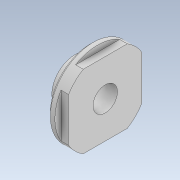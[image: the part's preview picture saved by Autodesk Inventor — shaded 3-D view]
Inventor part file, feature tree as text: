
AUTODESK INVENTOR PART (.ipt)
format: ipt  version: 2021 (Build 250183000, 183)  size: 128,512 bytes
history: native  units: mm
features: sketch x2, other x1, revolve x1, fillet x1, chamfer x1, extrude x1
ambient origin geometry x8: Origin, YZ Plane, XZ Plane, XY Plane, X Axis, Y Axis, Z Axis, Center Point
bodies: Body1 (feature_tree)
feature tree (7):
  other  "Sólido1"
  revolve  "Revolución1"  [1 undecoded]
  fillet  "Empalme1"  Radius=28.0mm
  chamfer  "Chaflán1"  Distance=8.0mm
  extrude  "Extrusión1"  TaperAngle=90.0deg  [1 undecoded]
  sketch  "Boceto1"  dims[d0=5.0mm d1=5.0mm d3=28.0mm]
  sketch  "Boceto2"  dims[d4=15.0mm d5=8.0mm d6=90.0deg d7=1.0mm d8=1.0mm d9=2.0mm d10=45.0deg d11=24.0mm d12=24.0mm d13=2.5mm d14=0.0mm]
note: 2 required parameter values undecoded (feature->parameter linkage not recoverable at this tier; creation-order binding heuristic only, values carry confidence <= 0.55)